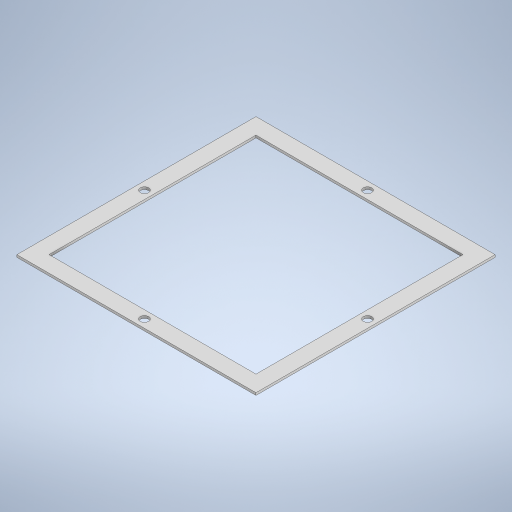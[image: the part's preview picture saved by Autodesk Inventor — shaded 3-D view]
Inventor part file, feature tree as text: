
AUTODESK INVENTOR PART (.ipt)
format: ipt  version: 2024.2 (Build 282272000, 272)  size: 265,216 bytes
history: native  units: in
note: dims shown in document units (in); Inventor stores cm internally (conversion verified against a paired STEP export)
features: extrude x2, sketch x2
ambient origin geometry x8: Origin, YZ Plane, XZ Plane, XY Plane, X Axis, Y Axis, Z Axis, Center Point
bodies: Solid1 (feature_tree)
feature tree (4):
  extrude  "Extrusion1"  Depth=3.5in
  extrude  "Extrusion2"  Depth=0.235in
  sketch  "Sketch1"  dims[d0=3.5in d1=3.5in]
  sketch  "Sketch2"  dims[d2=0.235in d3=0.235in d4=0.235in d5=0.235in d6=0.035in d7=0.0in d8=0.125in d9=0.1175in d10=1.75in d11=0.125in d12=0.1175in d13=0.125in d14=0.1175in d15=0.125in d16=0.1175in d17=0.0in d18=0.0in]
